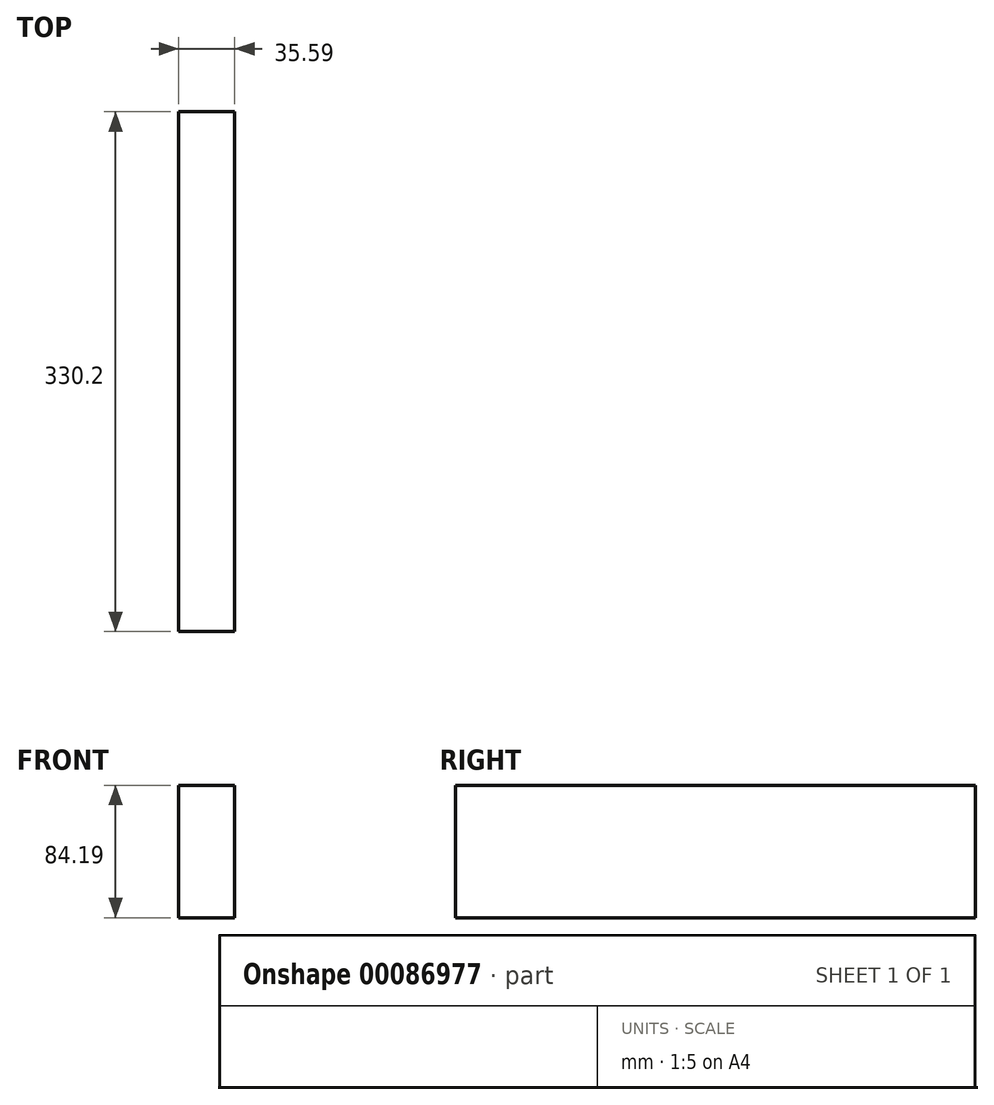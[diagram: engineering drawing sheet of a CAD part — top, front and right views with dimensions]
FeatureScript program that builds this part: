
annotation { "Feature Type Name" : "Feature", "Feature Type Description" : "" }
export const myFeature = defineFeature(function(context is Context, id is Id, definition is map)
    precondition{}
    {
        {
            var Q0;
            Q0=qCreatedBy(makeId("Front.planeOp"),FACE);
            var sketch = newSketch(context, id + "F0", { "sketchPlane" : qUnion([Q0])});
            skLineSegment(sketch, "E0", {"start": v(-45.19, 49.06) * mm, "end": v(-45.19, -35.13) * mm});
            skLineSegment(sketch, "E1", {"start": v(-45.19, -35.13) * mm, "end": v(-9.6, -35.13) * mm});
            skLineSegment(sketch, "E2", {"start": v(-9.6, -35.13) * mm, "end": v(-9.6, 49.06) * mm});
            skLineSegment(sketch, "E3", {"start": v(-9.6, 49.06) * mm, "end": v(-45.19, 49.06) * mm});
            skSolve(sketch);
        }
        {
            var Q0;
            Q0 = qSketchRegion(id + "F0", true);
            extrude(context, id + "F1", {"entities" : qUnion([Q0]), "depth" : 330.2 * mm});
        }
    });
